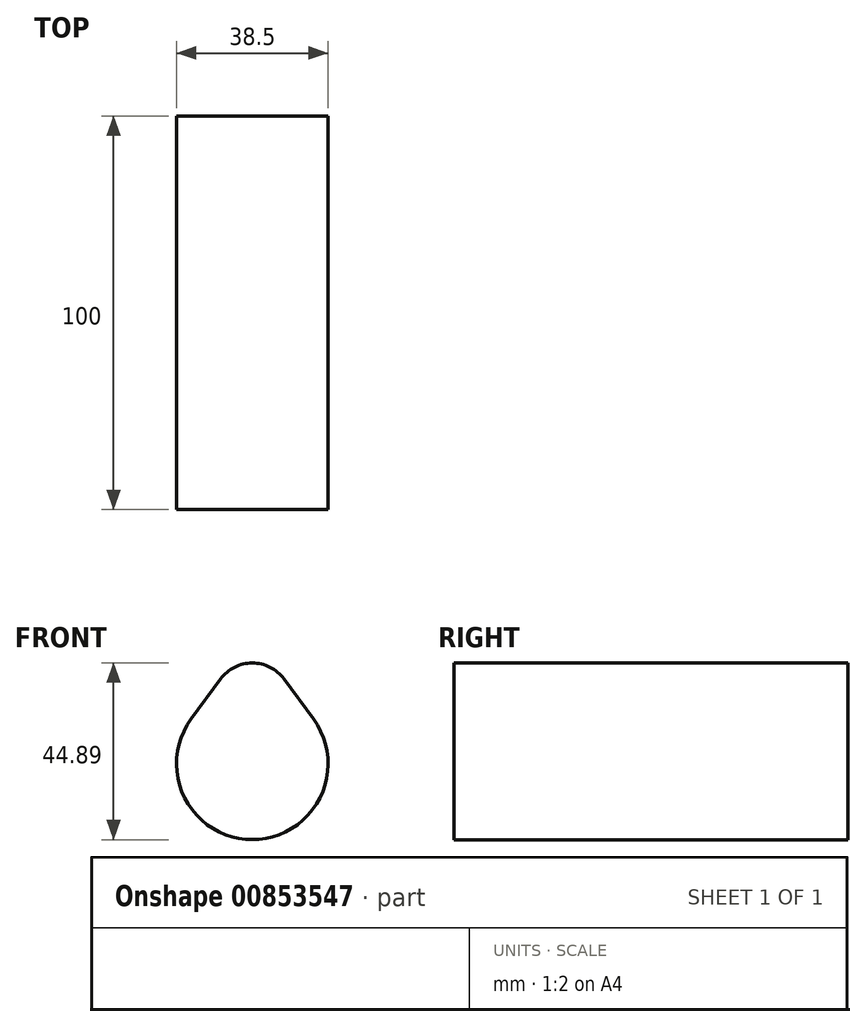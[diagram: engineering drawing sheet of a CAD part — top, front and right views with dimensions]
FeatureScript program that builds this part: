
annotation { "Feature Type Name" : "Feature", "Feature Type Description" : "" }
export const myFeature = defineFeature(function(context is Context, id is Id, definition is map)
    precondition{}
    {
        {
            var Q0;
            Q0=qCreatedBy(makeId("Front.planeOp"),FACE);
            var sketch = newSketch(context, id + "F0", { "sketchPlane" : qUnion([Q0])});
            skArc(sketch, "E0", {"start": v(-15.53, 11.38) * mm, "mid": v(0, -19.25) * mm, "end": v(15.53, 11.38) * mm});
            skLineSegment(sketch, "E1", {"start": v(-8.07, 21.56) * mm, "end": v(-15.53, 11.38) * mm});
            skLineSegment(sketch, "E2", {"start": v(15.53, 11.38) * mm, "end": v(8.06, 21.56) * mm});
            skPoint(sketch, "E3.visualSharp", {"position": v(0, 32.55) * mm});
            skArc(sketch, "E3.filletArc", {"start": v(8.06, 21.56) * mm, "mid": v(0, 25.64) * mm, "end": v(-8.07, 21.56) * mm});
            skLineSegment(sketch, "E4", {"start": v(-15.53, 11.38) * mm, "end": v(15.53, 11.38) * mm, "construction": true});
            skSolve(sketch);
        }
        {
            var Q0;
            Q0=makeQuery(id+"F0.imprint","IMPRINT",FACE,{"disambiguationData":[TD([[makeQuery(id+"F0.imprint","IMPRINT",EDGE,{"derivedFrom":sQuery(id+"F0.wireOp",EDGE,"E0")}),1.0]])]});
            extrude(context, id + "F1", {"entities" : qUnion([Q0]), "endBound" : BoundingType.SYMMETRIC, "depth" : 100 * mm, "offsetDistance" : 25 * mm});
        }
    });
